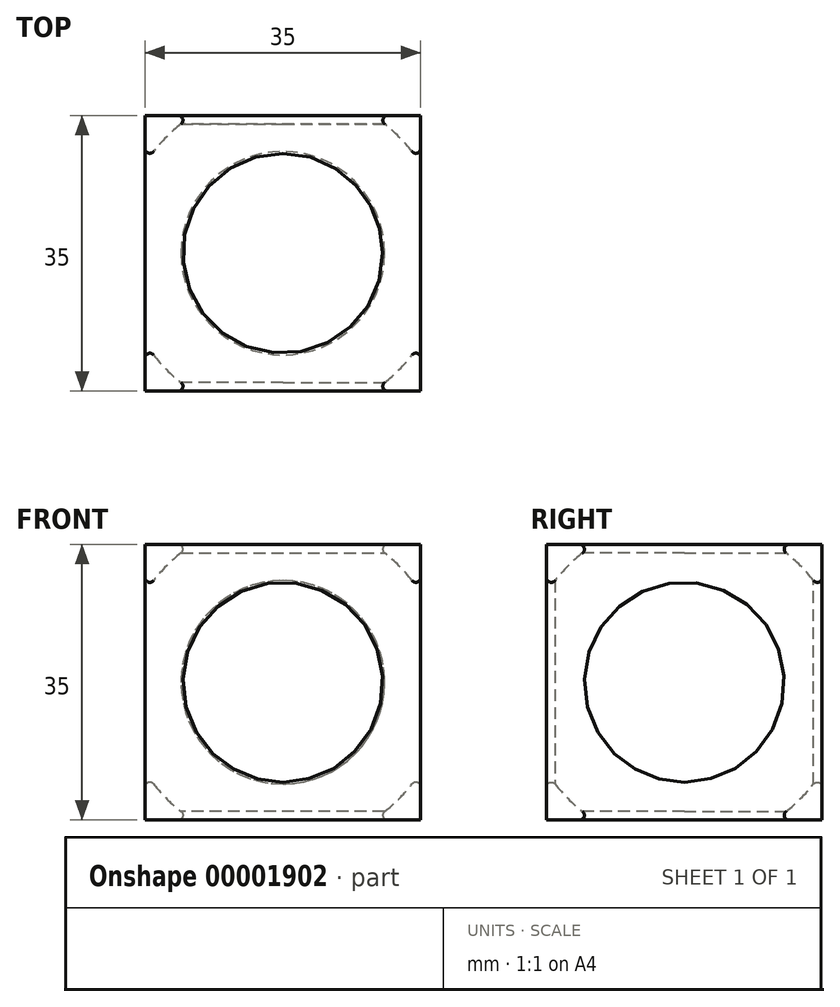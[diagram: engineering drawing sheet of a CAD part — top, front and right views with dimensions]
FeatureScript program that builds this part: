
annotation { "Feature Type Name" : "Feature", "Feature Type Description" : "" }
export const myFeature = defineFeature(function(context is Context, id is Id, definition is map)
    precondition{}
    {
        {
            var Q0;
            Q0=qCreatedBy(makeId("Top.planeOp"),FACE);
            var sketch = newSketch(context, id + "F0", { "sketchPlane" : qUnion([Q0])});
            skLineSegment(sketch, "E0.rect.bottom", {"start": v(10, 10) * mm, "end": v(-10, 10) * mm});
            skLineSegment(sketch, "E0.rect.top", {"start": v(10, -10) * mm, "end": v(-10, -10) * mm});
            skLineSegment(sketch, "E0.rect.left", {"start": v(10, 10) * mm, "end": v(10, -10) * mm});
            skLineSegment(sketch, "E0.rect.right", {"start": v(-10, 10) * mm, "end": v(-10, -10) * mm});
            skPoint(sketch, "E0.rect.middle", {"position": v(0, 0) * mm});
            skSolve(sketch);
        }
        {
            var Q0;
            Q0=qCreatedBy(makeId("Top.planeOp"),FACE);
            var sketch = newSketch(context, id + "F1", { "sketchPlane" : qUnion([Q0])});
            skArc(sketch, "E1", {"start": v(11.5, 0) * mm, "mid": v(0, 11.5) * mm, "end": v(-11.5, 0) * mm});
            skLineSegment(sketch, "E2", {"start": v(-11.5, 0) * mm, "end": v(11.5, 0) * mm});
            skArc(sketch, "E3.0", {"start": v(14, 0) * mm, "mid": v(0, 14) * mm, "end": v(-14, 0) * mm});
            skArc(sketch, "E4.0", {"start": v(19, 0) * mm, "mid": v(0, 19) * mm, "end": v(-19, 0) * mm});
            skLineSegment(sketch, "E5", {"start": v(14, 0) * mm, "end": v(19, 0) * mm});
            skLineSegment(sketch, "E6", {"start": v(-19, 0) * mm, "end": v(-14, 0) * mm});
            skSolve(sketch);
        }
        {
            var Q0;
            Q0 = qSketchRegion(id + "F0", true);
            extrude(context, id + "F2", {"entities" : qUnion([Q0]), "endBound" : BoundingType.SYMMETRIC, "depth" : 20 * mm});
        }
        {
            var Q0;
            Q0 = qSketchRegion(id + "F1", true);
            var Q1;
            Q1=sQuery(id+"F1.wireOp",EDGE,"E6");
            revolve(context, id + "F3", {"operationType" : NewBodyOperationType.REMOVE, "entities" : qUnion([Q0]), "axis" : qUnion([Q1]), "revolveType" : RevolveType.FULL, "oppositeDirection" : true});
        }
        {
            var Q0;
            Q0=qCreatedBy(makeId("Top.planeOp"),FACE);
            var sketch = newSketch(context, id + "F4", { "sketchPlane" : qUnion([Q0])});
            skArc(sketch, "E7.0", {"start": v(14.3, 0) * mm, "mid": v(0, 14.3) * mm, "end": v(-14.3, 0) * mm});
            skArc(sketch, "E8.0", {"start": v(17.3, 0) * mm, "mid": v(0, 17.3) * mm, "end": v(-17.3, 0) * mm});
            skLineSegment(sketch, "E9", {"start": v(-14.3, 0) * mm, "end": v(14.3, 0) * mm});
            skArc(sketch, "E10.0", {"start": v(23.3, 0) * mm, "mid": v(0, 23.3) * mm, "end": v(-23.3, 0) * mm});
            skLineSegment(sketch, "E11", {"start": v(-23.3, 0) * mm, "end": v(-17.3, 0) * mm});
            skLineSegment(sketch, "E12", {"start": v(17.3, 0) * mm, "end": v(23.3, 0) * mm});
            skSolve(sketch);
        }
        {
            var Q0;
            Q0=qCreatedBy(makeId("Top.planeOp"),FACE);
            var sketch = newSketch(context, id + "F5", { "sketchPlane" : qUnion([Q0])});
            skLineSegment(sketch, "E13.rect.bottom", {"start": v(12.5, 12.5) * mm, "end": v(-12.5, 12.5) * mm});
            skLineSegment(sketch, "E13.rect.top", {"start": v(12.5, -12.5) * mm, "end": v(-12.5, -12.5) * mm});
            skLineSegment(sketch, "E13.rect.left", {"start": v(12.5, 12.5) * mm, "end": v(12.5, -12.5) * mm});
            skLineSegment(sketch, "E13.rect.right", {"start": v(-12.5, 12.5) * mm, "end": v(-12.5, -12.5) * mm});
            skPoint(sketch, "E13.rect.middle", {"position": v(0, 0) * mm});
            skSolve(sketch);
        }
        {
            var Q0;
            Q0 = qSketchRegion(id + "F5", true);
            extrude(context, id + "F6", {"entities" : qUnion([Q0]), "endBound" : BoundingType.SYMMETRIC, "depth" : 25 * mm});
        }
        {
            var Q0;
            Q0 = qSketchRegion(id + "F4", true);
            var Q1;
            Q1=sQuery(id+"F4.wireOp",EDGE,"E11");
            revolve(context, id + "F7", {"operationType" : NewBodyOperationType.REMOVE, "entities" : qUnion([Q0]), "axis" : qUnion([Q1]), "revolveType" : RevolveType.FULL, "oppositeDirection" : true});
        }
        {
            var Q0;
            Q0=qCreatedBy(makeId("Top.planeOp"),FACE);
            var sketch = newSketch(context, id + "F8", { "sketchPlane" : qUnion([Q0])});
            skArc(sketch, "E14.0", {"start": v(17.6, 0) * mm, "mid": v(0, 17.6) * mm, "end": v(-17.6, 0) * mm});
            skLineSegment(sketch, "E15", {"start": v(-17.6, 0) * mm, "end": v(17.6, 0) * mm});
            skArc(sketch, "E16.0", {"start": v(20.6, 0) * mm, "mid": v(0, 20.6) * mm, "end": v(-20.6, 0) * mm});
            skArc(sketch, "E17.0", {"start": v(27.6, 0) * mm, "mid": v(0, 27.6) * mm, "end": v(-27.6, 0) * mm});
            skLineSegment(sketch, "E18", {"start": v(-27.6, 0) * mm, "end": v(-20.6, 0) * mm});
            skLineSegment(sketch, "E19", {"start": v(20.6, 0) * mm, "end": v(27.6, 0) * mm});
            skSolve(sketch);
        }
        {
            var Q0;
            Q0=qCreatedBy(makeId("Top.planeOp"),FACE);
            var sketch = newSketch(context, id + "F9", { "sketchPlane" : qUnion([Q0])});
            skLineSegment(sketch, "E20.rect.bottom", {"start": v(15, 15) * mm, "end": v(-15, 15) * mm});
            skLineSegment(sketch, "E20.rect.top", {"start": v(15, -15) * mm, "end": v(-15, -15) * mm});
            skLineSegment(sketch, "E20.rect.left", {"start": v(15, 15) * mm, "end": v(15, -15) * mm});
            skLineSegment(sketch, "E20.rect.right", {"start": v(-15, 15) * mm, "end": v(-15, -15) * mm});
            skPoint(sketch, "E20.rect.middle", {"position": v(0, 0) * mm});
            skSolve(sketch);
        }
        {
            var Q0;
            Q0 = qSketchRegion(id + "F9", true);
            extrude(context, id + "F10", {"entities" : qUnion([Q0]), "endBound" : BoundingType.SYMMETRIC, "depth" : 30 * mm});
        }
        {
            var Q0;
            Q0 = qSketchRegion(id + "F8", true);
            var Q1;
            Q1=sQuery(id+"F8.wireOp",EDGE,"E18");
            revolve(context, id + "F11", {"operationType" : NewBodyOperationType.REMOVE, "entities" : qUnion([Q0]), "axis" : qUnion([Q1]), "revolveType" : RevolveType.FULL, "oppositeDirection" : true});
        }
        {
            var Q0;
            Q0=makeQuery(id+"F11.boolean.opBoolean","INTERSECT",EDGE,{"derivedFrom":[makeQuery(id+"F10.opExtrude","CAP_FACE",FACE,{"disambiguationData":[OSD([sQuery(id+"F9.wireOp",EDGE,"E20.rect.bottom"),sQuery(id+"F9.wireOp",EDGE,"E20.rect.top"),sQuery(id+"F9.wireOp",EDGE,"E20.rect.left"),sQuery(id+"F9.wireOp",EDGE,"E20.rect.right")])],"isStart":true}),makeQuery(id+"F11.opRevolve","SWEPT_FACE",FACE,{"disambiguationData":[OSD([sQuery(id+"F8.wireOp",EDGE,"E14.0")])]})]});
            var Q1;
            Q1=makeQuery(id+"F7.boolean.opBoolean","INTERSECT",EDGE,{"derivedFrom":[makeQuery(id+"F6.opExtrude","CAP_FACE",FACE,{"disambiguationData":[OSD([sQuery(id+"F5.wireOp",EDGE,"E13.rect.bottom"),sQuery(id+"F5.wireOp",EDGE,"E13.rect.top"),sQuery(id+"F5.wireOp",EDGE,"E13.rect.left"),sQuery(id+"F5.wireOp",EDGE,"E13.rect.right")])],"isStart":true}),makeQuery(id+"F7.opRevolve","SWEPT_FACE",FACE,{"disambiguationData":[OSD([sQuery(id+"F4.wireOp",EDGE,"E7.0")])]})]});
            var Q2;
            Q2=makeQuery(id+"F3.boolean.opBoolean","INTERSECT",EDGE,{"derivedFrom":[makeQuery(id+"F2.opExtrude","CAP_FACE",FACE,{"disambiguationData":[OSD([sQuery(id+"F0.wireOp",EDGE,"E0.rect.bottom"),sQuery(id+"F0.wireOp",EDGE,"E0.rect.top"),sQuery(id+"F0.wireOp",EDGE,"E0.rect.left"),sQuery(id+"F0.wireOp",EDGE,"E0.rect.right")])],"isStart":true}),makeQuery(id+"F3.opRevolve","SWEPT_FACE",FACE,{"disambiguationData":[OSD([sQuery(id+"F1.wireOp",EDGE,"E1")])]})]});
            var Q3;
            Q3=makeQuery(id+"F3.boolean.opBoolean","INTERSECT",EDGE,{"derivedFrom":[makeQuery(id+"F2.opExtrude","SWEPT_FACE",FACE,{"disambiguationData":[OSD([sQuery(id+"F0.wireOp",EDGE,"E0.rect.right")])]}),makeQuery(id+"F3.opRevolve","SWEPT_FACE",FACE,{"disambiguationData":[OSD([sQuery(id+"F1.wireOp",EDGE,"E1")])]})]});
            var Q4;
            Q4=makeQuery(id+"F7.boolean.opBoolean","INTERSECT",EDGE,{"derivedFrom":[makeQuery(id+"F6.opExtrude","SWEPT_FACE",FACE,{"disambiguationData":[OSD([sQuery(id+"F5.wireOp",EDGE,"E13.rect.right")])]}),makeQuery(id+"F7.opRevolve","SWEPT_FACE",FACE,{"disambiguationData":[OSD([sQuery(id+"F4.wireOp",EDGE,"E7.0")])]})]});
            var Q5;
            Q5=makeQuery(id+"F11.boolean.opBoolean","INTERSECT",EDGE,{"derivedFrom":[makeQuery(id+"F10.opExtrude","SWEPT_FACE",FACE,{"disambiguationData":[OSD([sQuery(id+"F9.wireOp",EDGE,"E20.rect.right")])]}),makeQuery(id+"F11.opRevolve","SWEPT_FACE",FACE,{"disambiguationData":[OSD([sQuery(id+"F8.wireOp",EDGE,"E14.0")])]})]});
            var Q6;
            Q6=makeQuery(id+"F3.boolean.opBoolean","INTERSECT",EDGE,{"derivedFrom":[makeQuery(id+"F2.opExtrude","SWEPT_FACE",FACE,{"disambiguationData":[OSD([sQuery(id+"F0.wireOp",EDGE,"E0.rect.left")])]}),makeQuery(id+"F3.opRevolve","SWEPT_FACE",FACE,{"disambiguationData":[OSD([sQuery(id+"F1.wireOp",EDGE,"E1")])]})]});
            var Q7;
            Q7=makeQuery(id+"F3.boolean.opBoolean","INTERSECT",EDGE,{"derivedFrom":[makeQuery(id+"F2.opExtrude","SWEPT_FACE",FACE,{"disambiguationData":[OSD([sQuery(id+"F0.wireOp",EDGE,"E0.rect.bottom")])]}),makeQuery(id+"F3.opRevolve","SWEPT_FACE",FACE,{"disambiguationData":[OSD([sQuery(id+"F1.wireOp",EDGE,"E1")])]})]});
            var Q8;
            Q8=makeQuery(id+"F7.boolean.opBoolean","INTERSECT",EDGE,{"derivedFrom":[makeQuery(id+"F6.opExtrude","SWEPT_FACE",FACE,{"disambiguationData":[OSD([sQuery(id+"F5.wireOp",EDGE,"E13.rect.bottom")])]}),makeQuery(id+"F7.opRevolve","SWEPT_FACE",FACE,{"disambiguationData":[OSD([sQuery(id+"F4.wireOp",EDGE,"E7.0")])]})]});
            var Q9;
            Q9=makeQuery(id+"F11.boolean.opBoolean","INTERSECT",EDGE,{"derivedFrom":[makeQuery(id+"F10.opExtrude","SWEPT_FACE",FACE,{"disambiguationData":[OSD([sQuery(id+"F9.wireOp",EDGE,"E20.rect.bottom")])]}),makeQuery(id+"F11.opRevolve","SWEPT_FACE",FACE,{"disambiguationData":[OSD([sQuery(id+"F8.wireOp",EDGE,"E14.0")])]})]});
            var Q10;
            Q10=makeQuery(id+"F11.boolean.opBoolean","INTERSECT",EDGE,{"derivedFrom":[makeQuery(id+"F10.opExtrude","CAP_FACE",FACE,{"disambiguationData":[OSD([sQuery(id+"F9.wireOp",EDGE,"E20.rect.bottom"),sQuery(id+"F9.wireOp",EDGE,"E20.rect.top"),sQuery(id+"F9.wireOp",EDGE,"E20.rect.left"),sQuery(id+"F9.wireOp",EDGE,"E20.rect.right")])],"isStart":false}),makeQuery(id+"F11.opRevolve","SWEPT_FACE",FACE,{"disambiguationData":[OSD([sQuery(id+"F8.wireOp",EDGE,"E14.0")])]})]});
            var Q11;
            Q11=makeQuery(id+"F11.boolean.opBoolean","INTERSECT",EDGE,{"derivedFrom":[makeQuery(id+"F10.opExtrude","SWEPT_FACE",FACE,{"disambiguationData":[OSD([sQuery(id+"F9.wireOp",EDGE,"E20.rect.left")])]}),makeQuery(id+"F11.opRevolve","SWEPT_FACE",FACE,{"disambiguationData":[OSD([sQuery(id+"F8.wireOp",EDGE,"E14.0")])]})]});
            var Q12;
            Q12=makeQuery(id+"F7.boolean.opBoolean","INTERSECT",EDGE,{"derivedFrom":[makeQuery(id+"F6.opExtrude","SWEPT_FACE",FACE,{"disambiguationData":[OSD([sQuery(id+"F5.wireOp",EDGE,"E13.rect.left")])]}),makeQuery(id+"F7.opRevolve","SWEPT_FACE",FACE,{"disambiguationData":[OSD([sQuery(id+"F4.wireOp",EDGE,"E7.0")])]})]});
            var Q13;
            Q13=makeQuery(id+"F7.boolean.opBoolean","INTERSECT",EDGE,{"derivedFrom":[makeQuery(id+"F6.opExtrude","CAP_FACE",FACE,{"disambiguationData":[OSD([sQuery(id+"F5.wireOp",EDGE,"E13.rect.bottom"),sQuery(id+"F5.wireOp",EDGE,"E13.rect.top"),sQuery(id+"F5.wireOp",EDGE,"E13.rect.left"),sQuery(id+"F5.wireOp",EDGE,"E13.rect.right")])],"isStart":false}),makeQuery(id+"F7.opRevolve","SWEPT_FACE",FACE,{"disambiguationData":[OSD([sQuery(id+"F4.wireOp",EDGE,"E7.0")])]})]});
            var Q14;
            Q14=makeQuery(id+"F3.boolean.opBoolean","INTERSECT",EDGE,{"derivedFrom":[makeQuery(id+"F2.opExtrude","CAP_FACE",FACE,{"disambiguationData":[OSD([sQuery(id+"F0.wireOp",EDGE,"E0.rect.bottom"),sQuery(id+"F0.wireOp",EDGE,"E0.rect.top"),sQuery(id+"F0.wireOp",EDGE,"E0.rect.left"),sQuery(id+"F0.wireOp",EDGE,"E0.rect.right")])],"isStart":false}),makeQuery(id+"F3.opRevolve","SWEPT_FACE",FACE,{"disambiguationData":[OSD([sQuery(id+"F1.wireOp",EDGE,"E1")])]})]});
            var Q15;
            Q15=makeQuery(id+"F3.boolean.opBoolean","INTERSECT",EDGE,{"derivedFrom":[makeQuery(id+"F2.opExtrude","SWEPT_FACE",FACE,{"disambiguationData":[OSD([sQuery(id+"F0.wireOp",EDGE,"E0.rect.top")])]}),makeQuery(id+"F3.opRevolve","SWEPT_FACE",FACE,{"disambiguationData":[OSD([sQuery(id+"F1.wireOp",EDGE,"E1")])]})]});
            var Q16;
            Q16=makeQuery(id+"F7.boolean.opBoolean","INTERSECT",EDGE,{"derivedFrom":[makeQuery(id+"F6.opExtrude","SWEPT_FACE",FACE,{"disambiguationData":[OSD([sQuery(id+"F5.wireOp",EDGE,"E13.rect.top")])]}),makeQuery(id+"F7.opRevolve","SWEPT_FACE",FACE,{"disambiguationData":[OSD([sQuery(id+"F4.wireOp",EDGE,"E7.0")])]})]});
            var Q17;
            Q17=makeQuery(id+"F11.boolean.opBoolean","INTERSECT",EDGE,{"derivedFrom":[makeQuery(id+"F10.opExtrude","SWEPT_FACE",FACE,{"disambiguationData":[OSD([sQuery(id+"F9.wireOp",EDGE,"E20.rect.top")])]}),makeQuery(id+"F11.opRevolve","SWEPT_FACE",FACE,{"disambiguationData":[OSD([sQuery(id+"F8.wireOp",EDGE,"E14.0")])]})]});
            fillet(context, id + "F12", {"entities" : qUnion([Q0, Q1, Q2, Q3, Q4, Q5, Q6, Q7, Q8, Q9, Q10, Q11, Q12, Q13, Q14, Q15, Q16, Q17]), "radius" : 0.6 * mm, "tangentPropagation" : true, "allowEdgeOverflow" : false});
        }
        {
            var Q0;
            Q0=qCreatedBy(makeId("Top.planeOp"),FACE);
            var sketch = newSketch(context, id + "F13", { "sketchPlane" : qUnion([Q0])});
            skArc(sketch, "E21.0", {"start": v(20.9, 0) * mm, "mid": v(0, 20.9) * mm, "end": v(-20.9, 0) * mm});
            skLineSegment(sketch, "E22", {"start": v(-20.9, 0) * mm, "end": v(20.9, 0) * mm});
            skSolve(sketch);
        }
        {
            var Q0;
            Q0=qCreatedBy(makeId("Top.planeOp"),FACE);
            var sketch = newSketch(context, id + "F14", { "sketchPlane" : qUnion([Q0])});
            skLineSegment(sketch, "E23.rect.bottom", {"start": v(17.5, 17.5) * mm, "end": v(-17.5, 17.5) * mm});
            skLineSegment(sketch, "E23.rect.top", {"start": v(17.5, -17.5) * mm, "end": v(-17.5, -17.5) * mm});
            skLineSegment(sketch, "E23.rect.left", {"start": v(17.5, 17.5) * mm, "end": v(17.5, -17.5) * mm});
            skLineSegment(sketch, "E23.rect.right", {"start": v(-17.5, 17.5) * mm, "end": v(-17.5, -17.5) * mm});
            skPoint(sketch, "E23.rect.middle", {"position": v(0, 0) * mm});
            skSolve(sketch);
        }
        {
            var Q0;
            Q0 = qSketchRegion(id + "F14", true);
            extrude(context, id + "F15", {"entities" : qUnion([Q0]), "endBound" : BoundingType.SYMMETRIC, "depth" : 35 * mm});
        }
        {
            var Q0;
            Q0 = qSketchRegion(id + "F13", true);
            var Q1;
            Q1=sQuery(id+"F13.wireOp",EDGE,"E22");
            revolve(context, id + "F16", {"operationType" : NewBodyOperationType.REMOVE, "entities" : qUnion([Q0]), "axis" : qUnion([Q1]), "revolveType" : RevolveType.FULL, "oppositeDirection" : true});
        }
        {
            var Q0;
            Q0=makeQuery(id+"F16.boolean.opBoolean","INTERSECT",EDGE,{"derivedFrom":[makeQuery(id+"F15.opExtrude","SWEPT_FACE",FACE,{"disambiguationData":[OSD([sQuery(id+"F14.wireOp",EDGE,"E23.rect.right")])]}),makeQuery(id+"F16.opRevolve","SWEPT_FACE",FACE,{"disambiguationData":[OSD([sQuery(id+"F13.wireOp",EDGE,"E21.0")])]})]});
            var Q1;
            Q1=makeQuery(id+"F16.boolean.opBoolean","INTERSECT",EDGE,{"derivedFrom":[makeQuery(id+"F15.opExtrude","SWEPT_FACE",FACE,{"disambiguationData":[OSD([sQuery(id+"F14.wireOp",EDGE,"E23.rect.top")])]}),makeQuery(id+"F16.opRevolve","SWEPT_FACE",FACE,{"disambiguationData":[OSD([sQuery(id+"F13.wireOp",EDGE,"E21.0")])]})]});
            var Q2;
            Q2=makeQuery(id+"F16.boolean.opBoolean","INTERSECT",EDGE,{"derivedFrom":[makeQuery(id+"F15.opExtrude","CAP_FACE",FACE,{"disambiguationData":[OSD([sQuery(id+"F14.wireOp",EDGE,"E23.rect.bottom"),sQuery(id+"F14.wireOp",EDGE,"E23.rect.top"),sQuery(id+"F14.wireOp",EDGE,"E23.rect.left"),sQuery(id+"F14.wireOp",EDGE,"E23.rect.right")])],"isStart":false}),makeQuery(id+"F16.opRevolve","SWEPT_FACE",FACE,{"disambiguationData":[OSD([sQuery(id+"F13.wireOp",EDGE,"E21.0")])]})]});
            var Q3;
            Q3=makeQuery(id+"F16.boolean.opBoolean","INTERSECT",EDGE,{"derivedFrom":[makeQuery(id+"F15.opExtrude","CAP_FACE",FACE,{"disambiguationData":[OSD([sQuery(id+"F14.wireOp",EDGE,"E23.rect.bottom"),sQuery(id+"F14.wireOp",EDGE,"E23.rect.top"),sQuery(id+"F14.wireOp",EDGE,"E23.rect.left"),sQuery(id+"F14.wireOp",EDGE,"E23.rect.right")])],"isStart":true}),makeQuery(id+"F16.opRevolve","SWEPT_FACE",FACE,{"disambiguationData":[OSD([sQuery(id+"F13.wireOp",EDGE,"E21.0")])]})]});
            var Q4;
            Q4=makeQuery(id+"F16.boolean.opBoolean","INTERSECT",EDGE,{"derivedFrom":[makeQuery(id+"F15.opExtrude","SWEPT_FACE",FACE,{"disambiguationData":[OSD([sQuery(id+"F14.wireOp",EDGE,"E23.rect.bottom")])]}),makeQuery(id+"F16.opRevolve","SWEPT_FACE",FACE,{"disambiguationData":[OSD([sQuery(id+"F13.wireOp",EDGE,"E21.0")])]})]});
            var Q5;
            Q5=makeQuery(id+"F16.boolean.opBoolean","INTERSECT",EDGE,{"derivedFrom":[makeQuery(id+"F15.opExtrude","SWEPT_FACE",FACE,{"disambiguationData":[OSD([sQuery(id+"F14.wireOp",EDGE,"E23.rect.left")])]}),makeQuery(id+"F16.opRevolve","SWEPT_FACE",FACE,{"disambiguationData":[OSD([sQuery(id+"F13.wireOp",EDGE,"E21.0")])]})]});
            fillet(context, id + "F17", {"entities" : qUnion([Q0, Q1, Q2, Q3, Q4, Q5]), "radius" : 0.6 * mm, "tangentPropagation" : true, "allowEdgeOverflow" : false});
        }
    });
